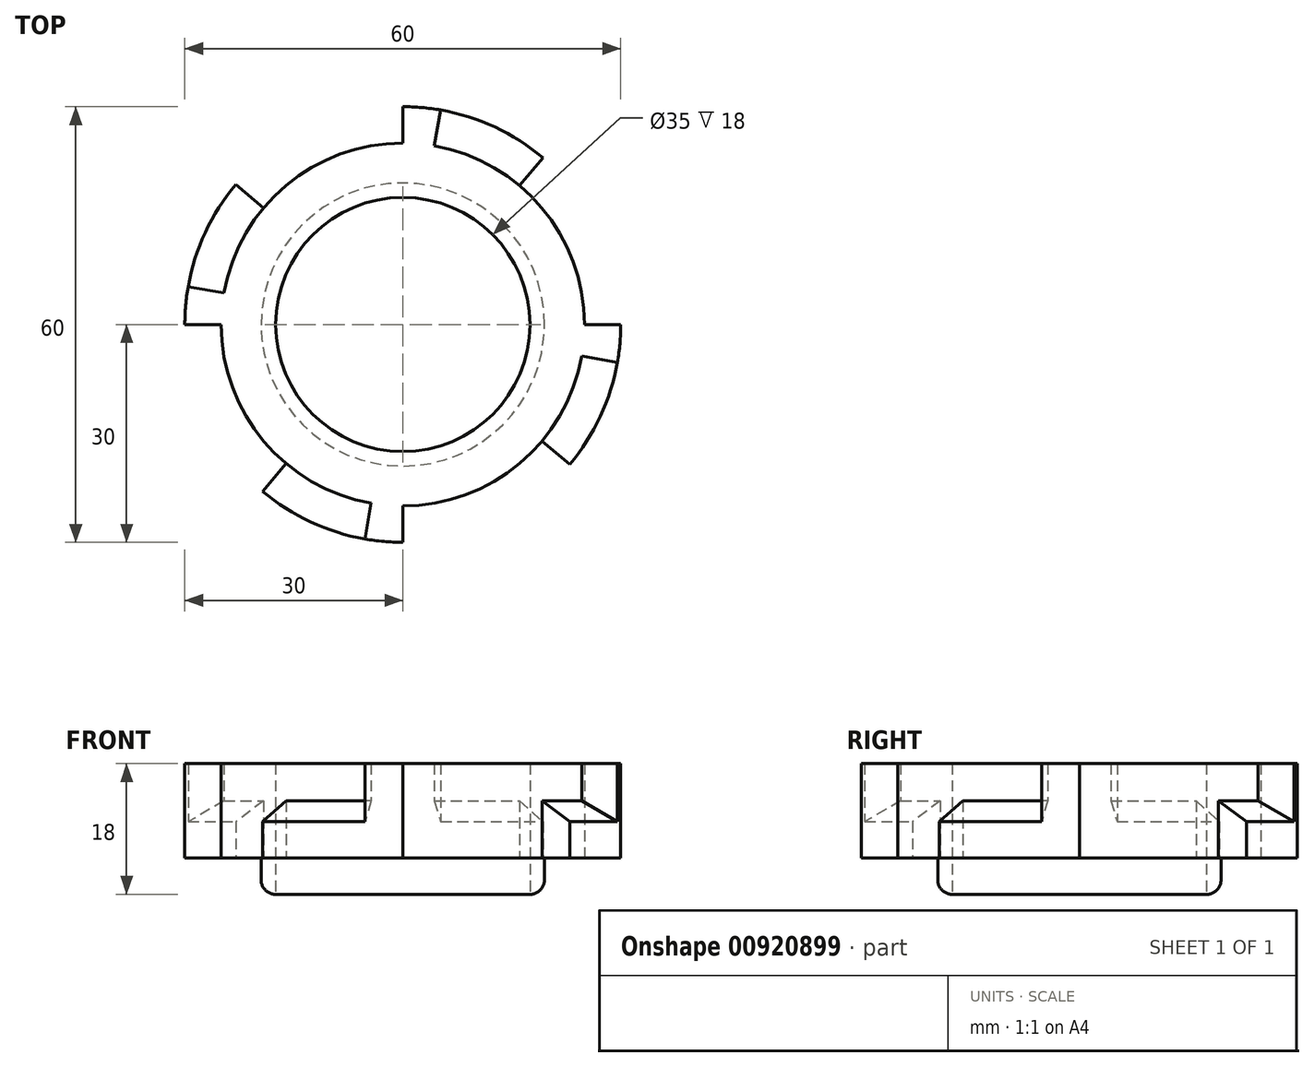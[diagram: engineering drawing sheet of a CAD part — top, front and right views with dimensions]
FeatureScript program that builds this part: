
annotation { "Feature Type Name" : "Feature", "Feature Type Description" : "" }
export const myFeature = defineFeature(function(context is Context, id is Id, definition is map)
    precondition{}
    {
        {
            var Q0;
            Q0=qCreatedBy(makeId("Front.planeOp"),FACE);
            var sketch = newSketch(context, id + "F0", { "sketchPlane" : qUnion([Q0])});
            skLineSegment(sketch, "E0", {"start": v(17.5, 0) * mm, "end": v(19.5, 0) * mm});
            skLineSegment(sketch, "E1", {"start": v(19.5, 0) * mm, "end": v(19.5, 5) * mm});
            skLineSegment(sketch, "E2", {"start": v(19.5, 5) * mm, "end": v(30, 5) * mm});
            skLineSegment(sketch, "E3", {"start": v(30, 5) * mm, "end": v(30, 10) * mm});
            skLineSegment(sketch, "E4", {"start": v(30, 10) * mm, "end": v(25, 12.89) * mm});
            skLineSegment(sketch, "E5", {"start": v(25, 12.89) * mm, "end": v(25, 18) * mm});
            skLineSegment(sketch, "E6", {"start": v(25, 18) * mm, "end": v(17.5, 18) * mm});
            skLineSegment(sketch, "E7", {"start": v(17.5, 18) * mm, "end": v(17.5, 0) * mm});
            skSolve(sketch);
        }
        {
            var Q0;
            Q0=qCreatedBy(makeId("Front.planeOp"),FACE);
            var sketch = newSketch(context, id + "F1", { "sketchPlane" : qUnion([Q0])});
            skLineSegment(sketch, "E8", {"start": v(0, 0) * mm, "end": v(0, 36.68) * mm});
            skSolve(sketch);
        }
        {
            var Q0;
            Q0=makeQuery(id+"F0.imprint","IMPRINT",FACE,{"disambiguationData":[TD([[makeQuery(id+"F0.imprint","IMPRINT",EDGE,{"derivedFrom":sQuery(id+"F0.wireOp",EDGE,"E0")}),1.0]])]});
            var Q1;
            Q1=sQuery(id+"F1.wireOp",EDGE,"E8");
            revolve(context, id + "F2", {"surfaceOperationType" : NewSurfaceOperationType.NEW, "entities" : qUnion([Q0]), "axis" : qUnion([Q1]), "revolveType" : RevolveType.FULL});
        }
        {
            var Q0;
            Q0=qCreatedBy(makeId("Top.planeOp"),FACE);
            var sketch = newSketch(context, id + "F3", { "sketchPlane" : qUnion([Q0])});
            skArc(sketch, "E9", {"start": v(-4.34, -24.62) * mm, "mid": v(-2.18, -24.9) * mm, "end": v(0, -25) * mm});
            skArc(sketch, "E10", {"start": v(-5.2, -29.54) * mm, "mid": v(-2.61, -29.89) * mm, "end": v(0, -30) * mm});
            skLineSegment(sketch, "E11", {"start": v(0, -25) * mm, "end": v(0, -30) * mm});
            skLineSegment(sketch, "E12", {"start": v(-4.34, -24.62) * mm, "end": v(-5.2, -29.54) * mm});
            skArc(sketch, "E13.1.0", {"start": v(29.54, -5.2) * mm, "mid": v(29.89, -2.61) * mm, "end": v(30, 0) * mm});
            skLineSegment(sketch, "E13.1.1", {"start": v(25, 0) * mm, "end": v(30, 0) * mm});
            skLineSegment(sketch, "E13.1.2", {"start": v(24.62, -4.34) * mm, "end": v(29.54, -5.2) * mm});
            skArc(sketch, "E13.1.3", {"start": v(24.62, -4.34) * mm, "mid": v(24.9, -2.18) * mm, "end": v(25, 0) * mm});
            skArc(sketch, "E13.2.0", {"start": v(5.2, 29.54) * mm, "mid": v(2.61, 29.89) * mm, "end": v(0, 30) * mm});
            skLineSegment(sketch, "E13.2.1", {"start": v(0, 25) * mm, "end": v(0, 30) * mm});
            skLineSegment(sketch, "E13.2.2", {"start": v(4.34, 24.62) * mm, "end": v(5.2, 29.54) * mm});
            skArc(sketch, "E13.2.3", {"start": v(4.34, 24.62) * mm, "mid": v(2.18, 24.9) * mm, "end": v(0, 25) * mm});
            skArc(sketch, "E13.3.0", {"start": v(-29.54, 5.2) * mm, "mid": v(-29.89, 2.61) * mm, "end": v(-30, 0) * mm});
            skLineSegment(sketch, "E13.3.1", {"start": v(-25, 0) * mm, "end": v(-30, 0) * mm});
            skLineSegment(sketch, "E13.3.2", {"start": v(-24.62, 4.34) * mm, "end": v(-29.54, 5.2) * mm});
            skArc(sketch, "E13.3.3", {"start": v(-24.62, 4.34) * mm, "mid": v(-24.9, 2.18) * mm, "end": v(-25, 0) * mm});
            skSolve(sketch);
        }
        {
            var Q0;
            Q0 = qSketchRegion(id + "F3", true);
            var Q1;
            Q1=makeQuery(id+"F2.opRevolve","SWEPT_FACE",FACE,{"disambiguationData":[OSD([sQuery(id+"F0.wireOp",EDGE,"E6")])]});
            var Q2;
            Q2=makeQuery(id+"F2.opRevolve","SWEPT_FACE",FACE,{"disambiguationData":[OSD([sQuery(id+"F0.wireOp",EDGE,"E2")])]});
            extrude(context, id + "F4", {"entities" : qUnion([Q0]), "operationType" : NewBodyOperationType.ADD, "endBound" : BoundingType.UP_TO_SURFACE, "depth" : 25 * mm, "endBoundEntityFace" : qUnion([Q1]), "offsetDistance" : 25 * mm, "hasSecondDirection" : true, "secondDirectionBound" : SecondDirectionBoundingType.UP_TO_SURFACE, "secondDirectionOppositeDirection" : false, "secondDirectionDepth" : 25 * mm, "secondDirectionBoundEntityFace" : qUnion([Q2])});
        }
        {
            var Q0;
            Q0=qCreatedBy(makeId("Top.planeOp"),FACE);
            var sketch = newSketch(context, id + "F5", { "sketchPlane" : qUnion([Q0])});
            skArc(sketch, "E14", {"start": v(0, -30) * mm, "mid": v(12.68, -27.19) * mm, "end": v(22.98, -19.28) * mm});
            skArc(sketch, "E15", {"start": v(0, -25) * mm, "mid": v(10.57, -22.66) * mm, "end": v(19.15, -16.07) * mm});
            skLineSegment(sketch, "E16", {"start": v(0, -25) * mm, "end": v(0, -30) * mm});
            skLineSegment(sketch, "E17", {"start": v(19.15, -16.07) * mm, "end": v(22.98, -19.28) * mm});
            skLineSegment(sketch, "E18.1.0", {"start": v(16.07, 19.15) * mm, "end": v(19.28, 22.98) * mm});
            skArc(sketch, "E18.1.1", {"start": v(25, 0) * mm, "mid": v(22.66, 10.57) * mm, "end": v(16.07, 19.15) * mm});
            skLineSegment(sketch, "E18.1.2", {"start": v(25, 0) * mm, "end": v(30, 0) * mm});
            skArc(sketch, "E18.1.3", {"start": v(30, 0) * mm, "mid": v(27.19, 12.68) * mm, "end": v(19.28, 22.98) * mm});
            skLineSegment(sketch, "E18.2.0", {"start": v(-19.15, 16.07) * mm, "end": v(-22.98, 19.28) * mm});
            skArc(sketch, "E18.2.1", {"start": v(0, 25) * mm, "mid": v(-10.57, 22.66) * mm, "end": v(-19.15, 16.07) * mm});
            skLineSegment(sketch, "E18.2.2", {"start": v(0, 25) * mm, "end": v(0, 30) * mm});
            skArc(sketch, "E18.2.3", {"start": v(0, 30) * mm, "mid": v(-12.68, 27.19) * mm, "end": v(-22.98, 19.28) * mm});
            skLineSegment(sketch, "E18.3.0", {"start": v(-16.07, -19.15) * mm, "end": v(-19.28, -22.98) * mm});
            skArc(sketch, "E18.3.1", {"start": v(-25, 0) * mm, "mid": v(-22.66, -10.57) * mm, "end": v(-16.07, -19.15) * mm});
            skLineSegment(sketch, "E18.3.2", {"start": v(-25, 0) * mm, "end": v(-30, 0) * mm});
            skArc(sketch, "E18.3.3", {"start": v(-30, 0) * mm, "mid": v(-27.19, -12.68) * mm, "end": v(-19.28, -22.98) * mm});
            skSolve(sketch);
        }
        {
            var Q0;
            Q0 = qSketchRegion(id + "F5", true);
            var Q1;
            Q1=makeQuery(id+"F4.boolean.opBoolean","MERGE",FACE,{"derivedFrom":[makeQuery(id+"F2.opRevolve","SWEPT_FACE",FACE,{"disambiguationData":[OSD([sQuery(id+"F0.wireOp",EDGE,"E6")])]}),makeQuery(id+"F4.opExtrude","CAP_FACE",FACE,{"disambiguationData":[OSD([sQuery(id+"F3.wireOp",EDGE,"E9"),sQuery(id+"F3.wireOp",EDGE,"E10"),sQuery(id+"F3.wireOp",EDGE,"E11"),sQuery(id+"F3.wireOp",EDGE,"E12")])],"isStart":false}),makeQuery(id+"F4.opExtrude","CAP_FACE",FACE,{"disambiguationData":[OSD([sQuery(id+"F3.wireOp",EDGE,"E13.1.0"),sQuery(id+"F3.wireOp",EDGE,"E13.1.1"),sQuery(id+"F3.wireOp",EDGE,"E13.1.2"),sQuery(id+"F3.wireOp",EDGE,"E13.1.3")])],"isStart":false}),makeQuery(id+"F4.opExtrude","CAP_FACE",FACE,{"disambiguationData":[OSD([sQuery(id+"F3.wireOp",EDGE,"E13.2.0"),sQuery(id+"F3.wireOp",EDGE,"E13.2.1"),sQuery(id+"F3.wireOp",EDGE,"E13.2.2"),sQuery(id+"F3.wireOp",EDGE,"E13.2.3")])],"isStart":false}),makeQuery(id+"F4.opExtrude","CAP_FACE",FACE,{"disambiguationData":[OSD([sQuery(id+"F3.wireOp",EDGE,"E13.3.0"),sQuery(id+"F3.wireOp",EDGE,"E13.3.1"),sQuery(id+"F3.wireOp",EDGE,"E13.3.2"),sQuery(id+"F3.wireOp",EDGE,"E13.3.3")])],"isStart":false})]});
            var Q2;
            Q2=makeQuery(id+"F2.opRevolve","SWEPT_FACE",FACE,{"disambiguationData":[OSD([sQuery(id+"F0.wireOp",EDGE,"E2")])]});
            extrude(context, id + "F6", {"entities" : qUnion([Q0]), "operationType" : NewBodyOperationType.REMOVE, "endBound" : BoundingType.UP_TO_SURFACE, "depth" : 25 * mm, "endBoundEntityFace" : qUnion([Q1]), "offsetDistance" : 25 * mm, "hasSecondDirection" : true, "secondDirectionBound" : SecondDirectionBoundingType.UP_TO_SURFACE, "secondDirectionOppositeDirection" : false, "secondDirectionDepth" : 25 * mm, "secondDirectionBoundEntityFace" : qUnion([Q2])});
        }
        {
            var Q0;
            Q0=makeQuery(id+"F2.opRevolve","SWEPT_EDGE",EDGE,{"disambiguationData":[OSD([sQuery(id+"F0.wireOp",EDGE,"E0"),sQuery(id+"F0.wireOp",EDGE,"E1")])]});
            fillet(context, id + "F7", {"entities" : qUnion([Q0]), "radius" : 2 * mm, "tangentPropagation" : true, "allowEdgeOverflow" : false});
        }
    });
